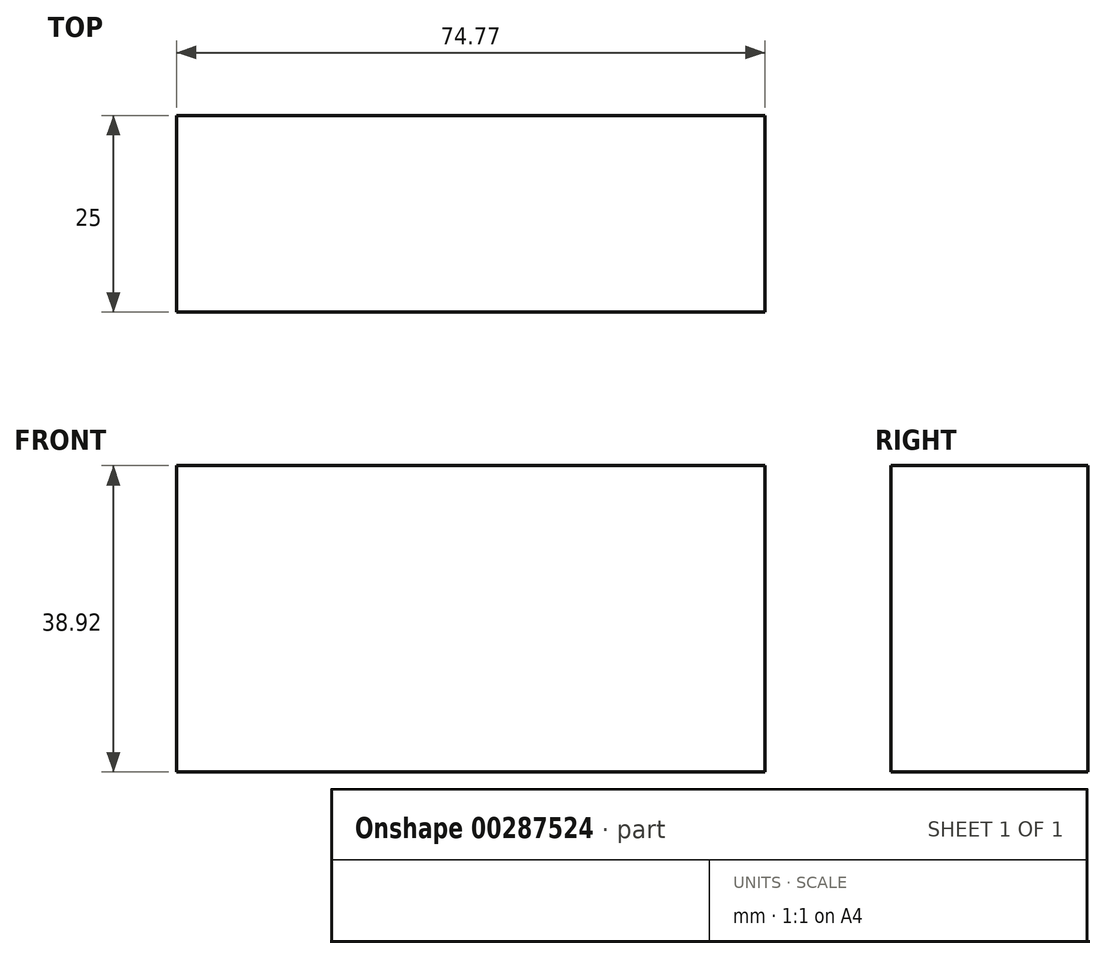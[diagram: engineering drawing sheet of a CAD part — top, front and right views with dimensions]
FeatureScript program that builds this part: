
annotation { "Feature Type Name" : "Feature", "Feature Type Description" : "" }
export const myFeature = defineFeature(function(context is Context, id is Id, definition is map)
    precondition{}
    {
        {
            var Q0;
            Q0=qCreatedBy(makeId("Front.planeOp"),FACE);
            var sketch = newSketch(context, id + "F0", { "sketchPlane" : qUnion([Q0])});
            skLineSegment(sketch, "E0.bottom", {"start": v(-61.87, 38.92) * mm, "end": v(-136.64, 38.92) * mm});
            skLineSegment(sketch, "E0.top", {"start": v(-61.87, 0) * mm, "end": v(-136.64, 0) * mm});
            skLineSegment(sketch, "E0.left", {"start": v(-61.87, 38.92) * mm, "end": v(-61.87, 0) * mm});
            skLineSegment(sketch, "E0.right", {"start": v(-136.64, 38.92) * mm, "end": v(-136.64, 0) * mm});
            skSolve(sketch);
        }
        {
            var Q0;
            Q0=makeQuery(id+"F0.imprint","IMPRINT",FACE,{"disambiguationData":[TD([[makeQuery(id+"F0.imprint","IMPRINT",EDGE,{"derivedFrom":sQuery(id+"F0.wireOp",EDGE,"E0.bottom")}),1.0]])]});
            extrude(context, id + "F1", {"entities" : qUnion([Q0]), "depth" : 25 * mm});
        }
    });
